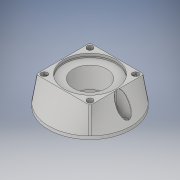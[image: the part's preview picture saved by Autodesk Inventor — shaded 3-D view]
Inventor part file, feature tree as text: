
AUTODESK INVENTOR PART (.ipt)
format: ipt  version: 2017 (Build 210142000, 142)  size: 739,328 bytes
history: native  units: in
note: dims shown in document units (in); Inventor stores cm internally (conversion verified against a paired STEP export)
features: fillet x1
ambient origin geometry x8: Origin, YZ Plane, XZ Plane, XY Plane, X Axis, Y Axis, Z Axis, Center Point
bodies: Solid1 (feature_tree)
feature tree (1):
  fillet  "Fillet3"  [1 undecoded]
note: 1 required parameter value undecoded (feature->parameter linkage not recoverable at this tier; creation-order binding heuristic only, values carry confidence <= 0.55)
